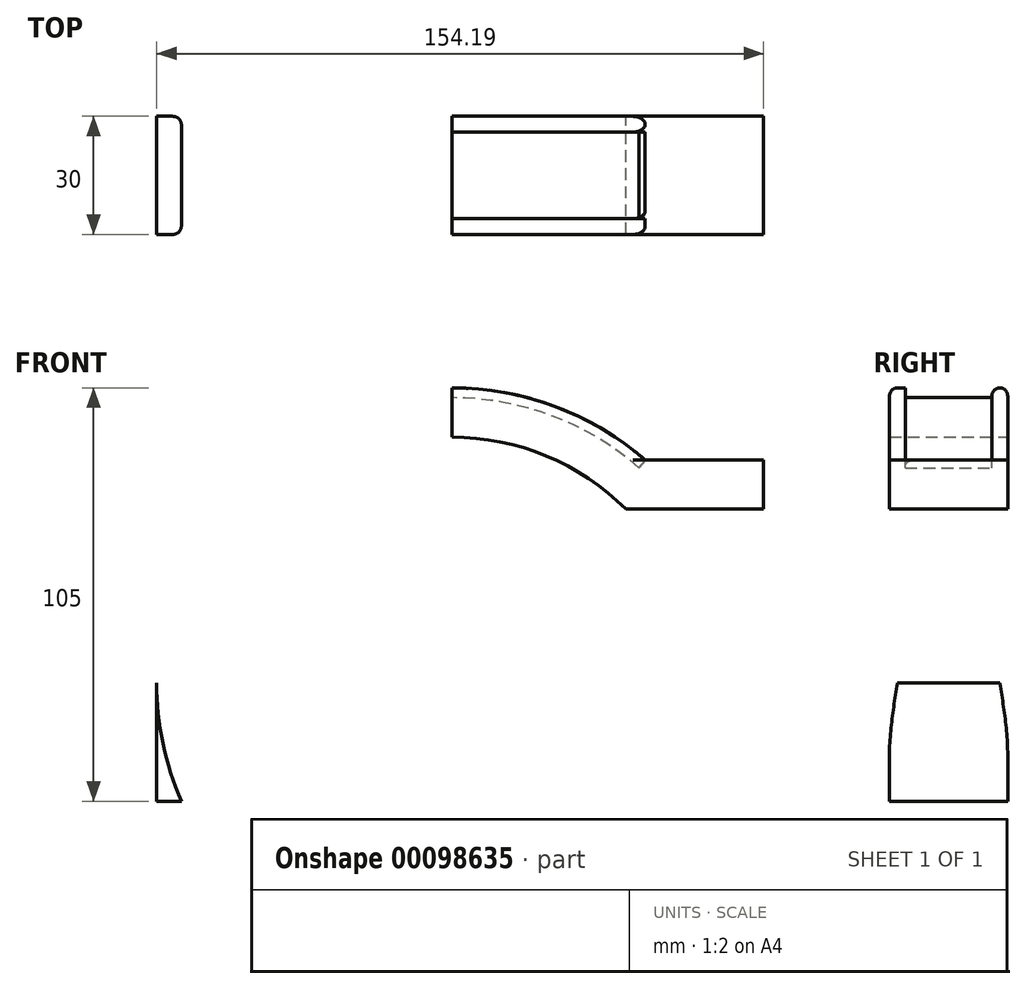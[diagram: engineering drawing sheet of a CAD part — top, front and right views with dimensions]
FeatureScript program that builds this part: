
annotation { "Feature Type Name" : "Feature", "Feature Type Description" : "" }
export const myFeature = defineFeature(function(context is Context, id is Id, definition is map)
    precondition{}
    {
        {
            var Q0;
            Q0=qCreatedBy(makeId("Front.planeOp"),FACE);
            var sketch = newSketch(context, id + "F0", { "sketchPlane" : qUnion([Q0])});
            skCircle(sketch, "E0", {"center": v(0, 0) * mm, "radius": 62.5 * mm});
            skCircle(sketch, "E1", {"center": v(0, 0) * mm, "radius": 75 * mm});
            skLineSegment(sketch, "E2", {"start": v(-62.5, 0) * mm, "end": v(-75, 0) * mm});
            skLineSegment(sketch, "E3", {"start": v(0, 0) * mm, "end": v(53.03, 53.03) * mm});
            skLineSegment(sketch, "E4.bottom", {"start": v(-75, 0) * mm, "end": v(-62.5, 0) * mm});
            skLineSegment(sketch, "E4.top", {"start": v(-75, -30) * mm, "end": v(-62.5, -30) * mm});
            skLineSegment(sketch, "E4.left", {"start": v(-75, 0) * mm, "end": v(-75, -30) * mm});
            skLineSegment(sketch, "E4.right", {"start": v(-62.5, 0) * mm, "end": v(-62.5, -30) * mm});
            skLineSegment(sketch, "E5.left", {"start": v(0, 62.5) * mm, "end": v(0, 75) * mm});
            skLineSegment(sketch, "E6.bottom", {"start": v(44.2, 44.2) * mm, "end": v(79.2, 44.2) * mm});
            skLineSegment(sketch, "E6.top", {"start": v(44.2, 56.7) * mm, "end": v(79.2, 56.7) * mm});
            skLineSegment(sketch, "E6.left", {"start": v(44.2, 44.2) * mm, "end": v(44.2, 56.7) * mm});
            skLineSegment(sketch, "E6.right", {"start": v(79.2, 44.2) * mm, "end": v(79.2, 56.7) * mm});
            skSolve(sketch);
        }
        {
            var Q0;
            {var subQ0=sQuery(id+"F0.wireOp",EDGE,"E4.bottom");Q0=makeQuery(id+"F0.imprint","IMPRINT",FACE,{"disambiguationData":[TD([[makeQuery(id+"F0.imprint","IMPRINT",EDGE,{"derivedFrom":subQ0}),-1.0]])]});}
            var Q1;
            {var subQ0=sQuery(id+"F0.wireOp",EDGE,"E4.left");Q1=makeQuery(id+"F0.imprint","IMPRINT",FACE,{"disambiguationData":[TD([[makeQuery(id+"F0.imprint","IMPRINT",EDGE,{"derivedFrom":subQ0}),1.0]])]});}
            var Q2;
            {var subQ0=sQuery(id+"F0.wireOp",EDGE,"E4.bottom");Q2=makeQuery(id+"F0.imprint","IMPRINT",FACE,{"disambiguationData":[TD([[makeQuery(id+"F0.imprint","IMPRINT",EDGE,{"derivedFrom":subQ0}),1.0]])]});}
            var Q3;
            {var subQ0=sQuery(id+"F0.wireOp",EDGE,"E5.left");Q3=makeQuery(id+"F0.imprint","IMPRINT",FACE,{"disambiguationData":[TD([[makeQuery(id+"F0.imprint","IMPRINT",EDGE,{"derivedFrom":subQ0}),-1.0]])]});}
            var Q4;
            {var subQ3=sQuery(id+"F0.wireOp",EDGE,"E3");var subQ5=sQuery(id+"F0.wireOp",EDGE,"E1");var subQ6=makeQuery(id+"F0.imprint","INTERSECT",VERTEX,{"derivedFrom":[subQ5,subQ3]});Q4=makeQuery(id+"F0.imprint","IMPRINT",FACE,{"disambiguationData":[TD([[makeQuery(id+"F0.imprint","IMPRINT",EDGE,{"disambiguationData":[TD([[subQ6,-1.0]])],"derivedFrom":subQ5}),1.0]])]});}
            var Q5;
            {var subQ0=sQuery(id+"F0.wireOp",EDGE,"E5.top");Q5=makeQuery(id+"F0.imprint","IMPRINT",FACE,{"disambiguationData":[TD([[makeQuery(id+"F0.imprint","IMPRINT",EDGE,{"derivedFrom":subQ0}),-1.0]])]});}
            var Q6;
            {var subQ0=sQuery(id+"F0.wireOp",EDGE,"E6.right");Q6=makeQuery(id+"F0.imprint","IMPRINT",FACE,{"disambiguationData":[TD([[makeQuery(id+"F0.imprint","IMPRINT",EDGE,{"derivedFrom":subQ0}),1.0]])]});}
            var Q7;
            {var subQ0=sQuery(id+"F0.wireOp",EDGE,"E3");var subQ1=sQuery(id+"F0.wireOp",EDGE,"E1");var subQ2=makeQuery(id+"F0.imprint","INTERSECT",VERTEX,{"derivedFrom":[subQ1,subQ0]});Q7=makeQuery(id+"F0.imprint","IMPRINT",FACE,{"disambiguationData":[TD([[makeQuery(id+"F0.imprint","IMPRINT",EDGE,{"disambiguationData":[TD([[subQ2,1.0]])],"derivedFrom":subQ1}),1.0]])]});}
            extrude(context, id + "F1", {"entities" : qUnion([Q0, Q1, Q2, Q3, Q4, Q5, Q6, Q7]), "endBound" : BoundingType.SYMMETRIC, "depth" : 30 * mm});
        }
        {
            var Q0;
            Q0=qCreatedBy(makeId("Front.planeOp"),FACE);
            var sketch = newSketch(context, id + "F2", { "sketchPlane" : qUnion([Q0])});
            skCircle(sketch, "E7", {"center": v(0, 0) * mm, "radius": 75 * mm});
            skCircle(sketch, "E8", {"center": v(0, 0) * mm, "radius": 72.5 * mm});
            skLineSegment(sketch, "E9", {"start": v(0, 0) * mm, "end": v(49.2, 56.6) * mm});
            skLineSegment(sketch, "E10", {"start": v(0, 0) * mm, "end": v(-75, 0) * mm});
            skSolve(sketch);
        }
        {
            var Q0;
            {var subQ0=sQuery(id+"F2.wireOp",EDGE,"E9");var subQ1=sQuery(id+"F2.wireOp",EDGE,"E7");var subQ2=makeQuery(id+"F2.imprint","INTERSECT",VERTEX,{"derivedFrom":[subQ1,subQ0]});Q0=makeQuery(id+"F2.imprint","IMPRINT",FACE,{"disambiguationData":[TD([[makeQuery(id+"F2.imprint","IMPRINT",EDGE,{"disambiguationData":[TD([[subQ2,-1.0]])],"derivedFrom":subQ1}),1.0]])]});}
            extrude(context, id + "F3", {"entities" : qUnion([Q0]), "operationType" : NewBodyOperationType.REMOVE, "endBound" : BoundingType.SYMMETRIC, "depth" : 22 * mm});
        }
        {
            var Q0;
            Q0=makeQuery(id+"F1.opExtrude","CAP_EDGE",EDGE,{"disambiguationData":[OSD([sQuery(id+"F0.wireOp",EDGE,"E1")])],"isStart":true});
            var Q1;
            {var subQ0=sQuery(id+"F2.wireOp",EDGE,"E7");Q1=makeQuery(id+"F3.boolean.opBoolean","COPY",EDGE,{"disambiguationData":[topologyDisambiguationEdgeConnected([makeQuery(id+"F1.opExtrude","SWEPT_FACE",FACE,{"disambiguationData":[OSD([sQuery(id+"F0.wireOp",EDGE,"E1")])]})])],"derivedFrom":makeQuery(id+"F3.opExtrude","CAP_EDGE",EDGE,{"disambiguationData":[OSD([subQ0])],"isStart":true})});}
            var Q2;
            {var subQ0=sQuery(id+"F2.wireOp",EDGE,"E7");Q2=makeQuery(id+"F3.boolean.opBoolean","COPY",EDGE,{"disambiguationData":[topologyDisambiguationEdgeConnected([makeQuery(id+"F1.opExtrude","SWEPT_FACE",FACE,{"disambiguationData":[OSD([sQuery(id+"F0.wireOp",EDGE,"E1")])]})])],"derivedFrom":makeQuery(id+"F3.opExtrude","CAP_EDGE",EDGE,{"disambiguationData":[OSD([subQ0])],"isStart":false})});}
            var Q3;
            Q3=makeQuery(id+"F1.opExtrude","CAP_EDGE",EDGE,{"disambiguationData":[OSD([sQuery(id+"F0.wireOp",EDGE,"E1")])],"isStart":false});
            fillet(context, id + "F4", {"entities" : qUnion([Q0, Q1, Q2, Q3]), "radius" : 2 * mm, "tangentPropagation" : true, "allowEdgeOverflow" : false});
        }
    });
